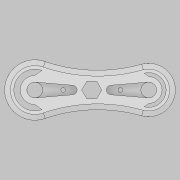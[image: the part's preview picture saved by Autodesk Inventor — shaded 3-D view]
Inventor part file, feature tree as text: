
AUTODESK INVENTOR PART (.ipt)
format: ipt  version: 2022.2 (Build 262287010, 287A)  size: 245,248 bytes
history: native  units: mm
features: extrude x6, sketch x5, other x1, chamfer x1
ambient origin geometry x8: Origin, YZ Plane, XZ Plane, XY Plane, X Axis, Y Axis, Z Axis, Center Point
bodies: Body1 (feature_tree)
feature tree (13):
  other  "Sólido1"
  extrude  "Extrusión1"  Depth=49.0mm
  extrude  "Extrusión2"  Depth=8.5mm
  extrude  "Extrusión3"  Depth=23.0mm
  extrude  "Extrusión4"  Depth=11.1mm
  extrude  "Extrusión5"  Depth=10.0mm
  extrude  "Extrusión6"  Depth=11.5mm
  chamfer  "Chaflán1"  Distance=4.0mm
  sketch  "Boceto1"  dims[d2=7.5mm d3=49.0mm]
  sketch  "Boceto2"  dims[d4=8.5mm d5=8.5mm]
  sketch  "Boceto4"  dims[d6=26.0mm d7=23.0mm]
  sketch  "Boceto5"  dims[d12=12.2mm d13=11.1mm]
  sketch  "Boceto6"  dims[d14=9.0mm d15=0.0mm d16=12.5mm d17=11.5mm d18=4.0mm d19=4.0mm d20=10.0mm d21=0.0mm d22=6.8mm d28=4.1mm d30=21.6mm d31=2.5mm d32=0.0mm d33=6.8mm d34=2.0mm d35=12.2mm d36=2.5mm d37=0.0mm d38=19.8mm d39=21.0mm d40=4.6mm d41=0.0mm d42=9.0mm d43=9.0mm d44=6.0mm d45=0.0mm d46=0.0mm d47=2.5mm d48=2.0mm d49=45.0deg]
